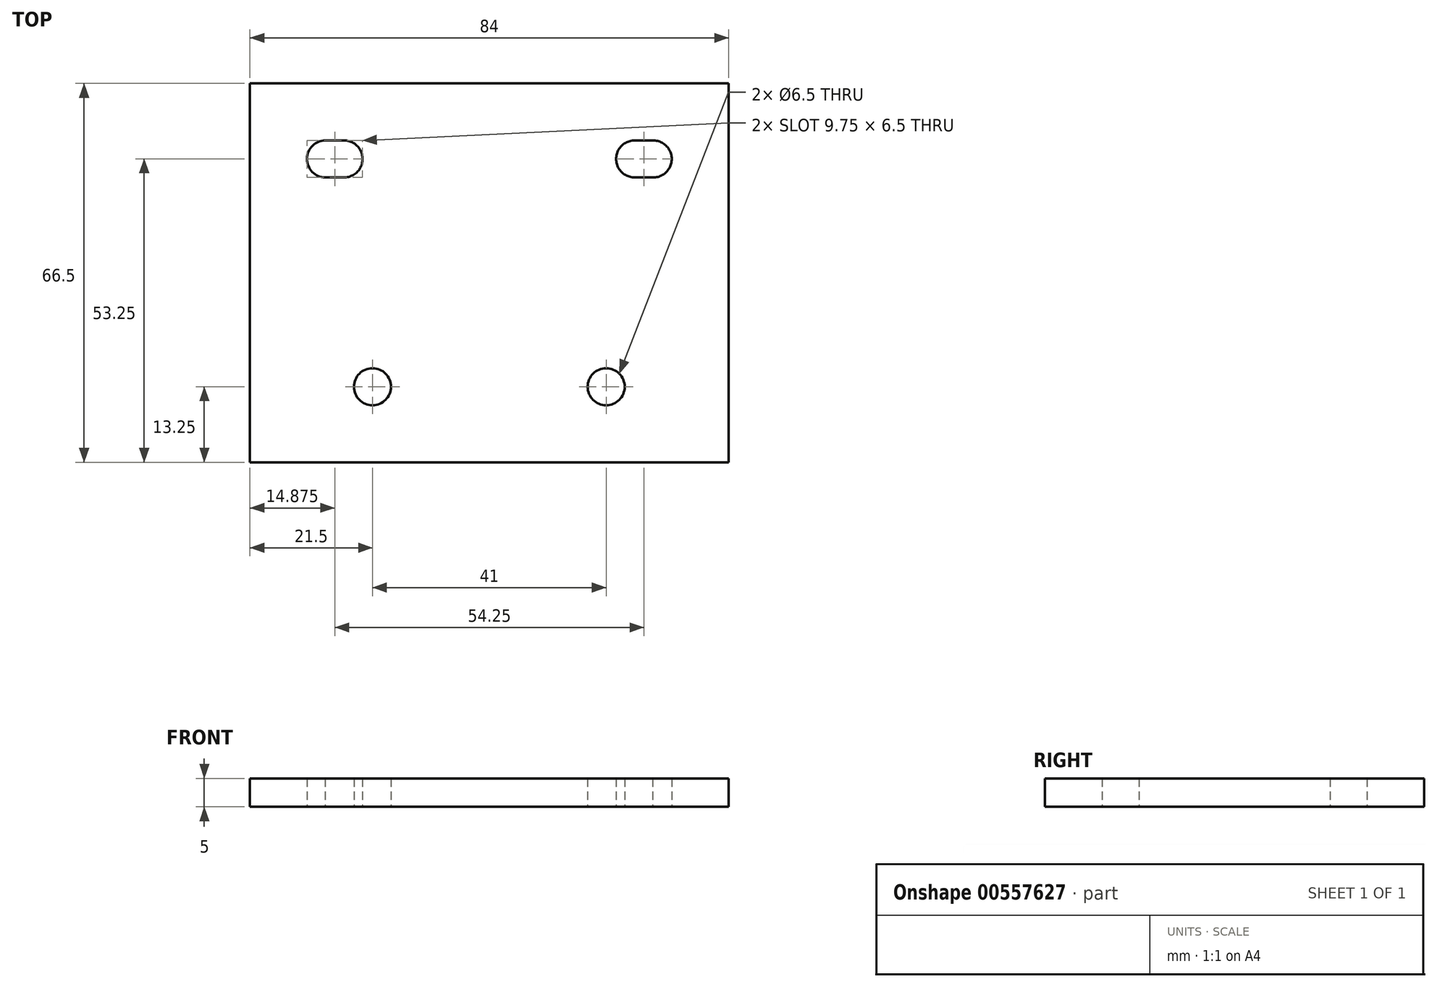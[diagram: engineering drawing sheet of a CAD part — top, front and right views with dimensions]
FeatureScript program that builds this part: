
annotation { "Feature Type Name" : "Feature", "Feature Type Description" : "" }
export const myFeature = defineFeature(function(context is Context, id is Id, definition is map)
    precondition{}
    {
        {
            var Q0;
            Q0=qCreatedBy(makeId("Top.planeOp"),FACE);
            var sketch = newSketch(context, id + "F0", { "sketchPlane" : qUnion([Q0])});
            skLineSegment(sketch, "E0", {"start": v(0, 0) * mm, "end": v(20.5, 0) * mm});
            skLineSegment(sketch, "E1", {"start": v(0, 0) * mm, "end": v(-20.5, 0) * mm});
            skCircle(sketch, "E2", {"center": v(-20.5, 0) * mm, "radius": 3.25 * mm});
            skCircle(sketch, "E3", {"center": v(20.5, 0) * mm, "radius": 3.25 * mm});
            skLineSegment(sketch, "E4", {"start": v(0, 0) * mm, "end": v(0, 40) * mm});
            skLineSegment(sketch, "E5", {"start": v(0, 40) * mm, "end": v(25.5, 40) * mm});
            skLineSegment(sketch, "E6", {"start": v(0, 40) * mm, "end": v(-25.5, 40) * mm});
            skArc(sketch, "E7", {"start": v(-25.53, 36.75) * mm, "mid": v(-22.25, 39.99) * mm, "end": v(-25.5, 43.25) * mm});
            skArc(sketch, "E8", {"start": v(25.5, 43.25) * mm, "mid": v(22.25, 40) * mm, "end": v(25.5, 36.75) * mm});
            skArc(sketch, "E9", {"start": v(-28.75, 43.25) * mm, "mid": v(-32, 40.03) * mm, "end": v(-28.8, 36.75) * mm});
            skArc(sketch, "E10", {"start": v(28.72, 36.75) * mm, "mid": v(32, 40.03) * mm, "end": v(28.67, 43.25) * mm});
            skLineSegment(sketch, "E11", {"start": v(28.67, 43.25) * mm, "end": v(25.5, 43.25) * mm});
            skLineSegment(sketch, "E12", {"start": v(28.78, 36.75) * mm, "end": v(25.5, 36.75) * mm});
            skLineSegment(sketch, "E13", {"start": v(-25.47, 36.75) * mm, "end": v(-28.8, 36.75) * mm});
            skLineSegment(sketch, "E14", {"start": v(-28.75, 43.25) * mm, "end": v(-25.5, 43.25) * mm});
            skLineSegment(sketch, "E15.bottom", {"start": v(-42, -13.25) * mm, "end": v(42, -13.25) * mm});
            skLineSegment(sketch, "E15.top", {"start": v(-42, 53.25) * mm, "end": v(42, 53.25) * mm});
            skLineSegment(sketch, "E15.left", {"start": v(-42, -13.25) * mm, "end": v(-42, 53.25) * mm});
            skLineSegment(sketch, "E15.right", {"start": v(42, -13.25) * mm, "end": v(42, 53.25) * mm});
            skSolve(sketch);
        }
        {
            var Q0;
            Q0=makeQuery(id+"F0.imprint","IMPRINT",FACE,{"disambiguationData":[TD([[makeQuery(id+"F0.imprint","IMPRINT",EDGE,{"derivedFrom":sQuery(id+"F0.wireOp",EDGE,"E2")}),-1.0]])]});
            extrude(context, id + "F1", {"entities" : qUnion([Q0]), "depth" : 5 * mm, "offsetDistance" : 25 * mm});
        }
    });
